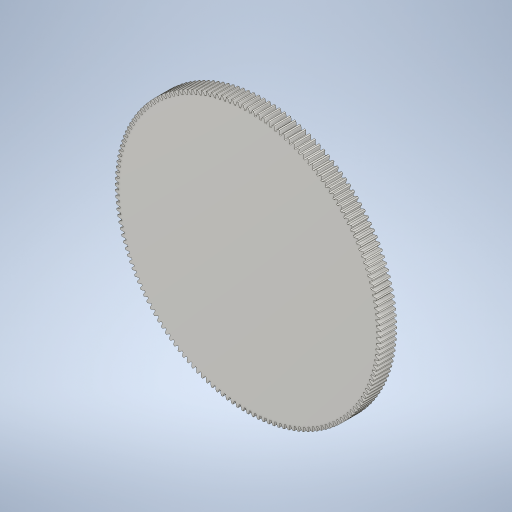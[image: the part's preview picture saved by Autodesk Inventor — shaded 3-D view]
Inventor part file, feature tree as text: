
AUTODESK INVENTOR PART (.ipt)
format: ipt  version: 2023 (Build 270158000, 158)  size: 843,776 bytes
history: native  units: mm (DEFAULTED — no unit token found)
features: plane x3, other x3, sketch x2, extrude x1
ambient origin geometry x8: Origin, YZ Plane, XZ Plane, XY Plane, X Axis, Y Axis, Z Axis, Center Point
bodies: Solid1 (feature_tree)
feature tree (9):
  extrude  "Extrusion1"  Depth=20.0mm TaperAngle=0.0deg
  plane  "Work Plane2"
  plane  "Work Plane8"
  plane  "Work Plane9"
  other  "Spur Gear"
  sketch  "Sketch1"  dims[d0=320.0mm d1=20.0mm d2=0.0mm]
  sketch  "Sketch2"  dims[d3=320.0mm d4=10.0mm d5=0.0mm d16=200.0mm d17=0.0mm d34=0.19635mm d39=0.0mm d41=0.0mm d43=200.0mm d46=200.0mm d47=0.0mm d48=0.0mm]
  other  "Srf1"
  other  "Pitch Diameter"
